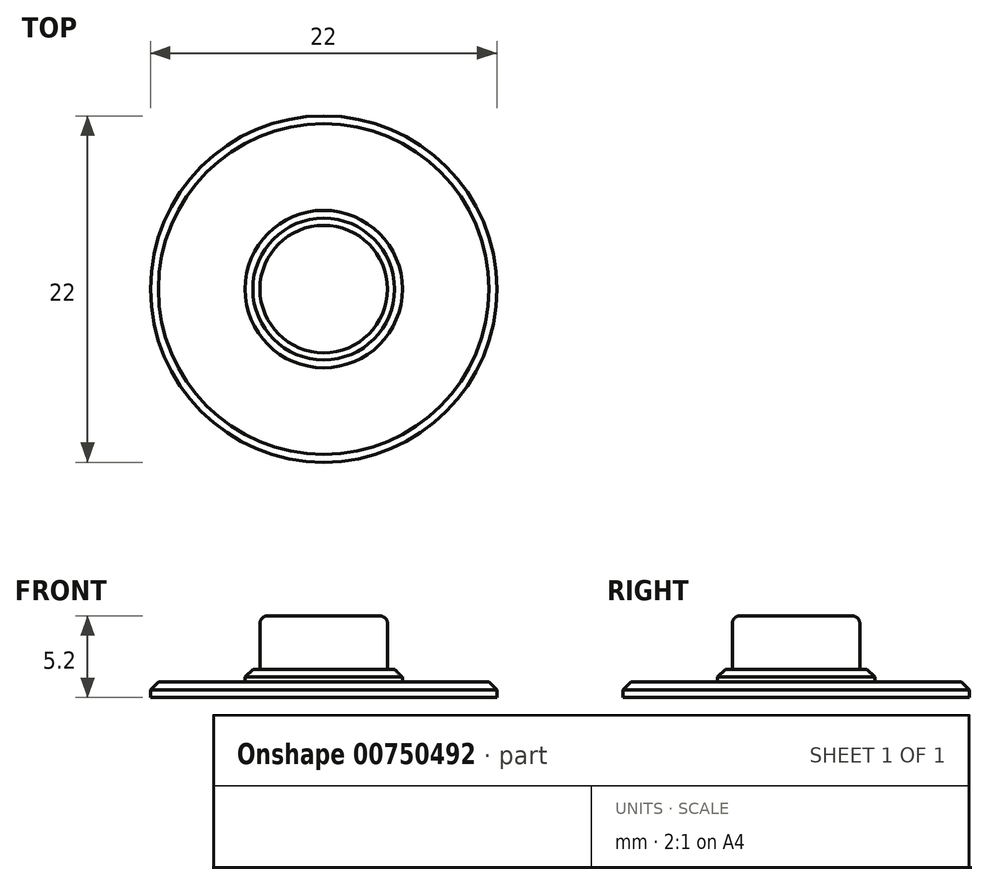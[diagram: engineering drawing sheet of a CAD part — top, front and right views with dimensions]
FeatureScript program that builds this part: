
annotation { "Feature Type Name" : "Feature", "Feature Type Description" : "" }
export const myFeature = defineFeature(function(context is Context, id is Id, definition is map)
    precondition{}
    {
        {
            var Q0;
            Q0=qCreatedBy(makeId("Top.planeOp"),FACE);
            var sketch = newSketch(context, id + "F0", { "sketchPlane" : qUnion([Q0])});
            skCircle(sketch, "E0", {"center": v(0, 0) * mm, "radius": 11 * mm});
            skCircle(sketch, "E1", {"center": v(0, 0) * mm, "radius": 4.05 * mm});
            skCircle(sketch, "E2", {"center": v(0, 0) * mm, "radius": 5 * mm});
            skSolve(sketch);
        }
        {
            var Q0;
            Q0=makeQuery(id+"F0.imprint","IMPRINT",FACE,{"disambiguationData":[TD([[makeQuery(id+"F0.imprint","IMPRINT",EDGE,{"derivedFrom":sQuery(id+"F0.wireOp",EDGE,"E0")}),1.0]])]});
            extrude(context, id + "F1", {"entities" : qUnion([Q0]), "depth" : 1 * mm, "offsetDistance" : 25 * mm});
        }
        {
            var Q0;
            Q0=makeQuery(id+"F1.opExtrude","CAP_EDGE",EDGE,{"disambiguationData":[OSD([sQuery(id+"F0.wireOp",EDGE,"E0")])],"isStart":false});
            chamfer(context, id + "F2", {"entities" : qUnion([Q0]), "width" : 0.5 * mm, "tangentPropagation" : true});
        }
        {
            var Q0;
            Q0=makeQuery(id+"F0.imprint","IMPRINT",FACE,{"disambiguationData":[TD([[makeQuery(id+"F0.imprint","IMPRINT",EDGE,{"derivedFrom":sQuery(id+"F0.wireOp",EDGE,"E1")}),-1.0]])]});
            extrude(context, id + "F3", {"entities" : qUnion([Q0]), "operationType" : NewBodyOperationType.ADD, "depth" : 1.8 * mm, "offsetDistance" : 25 * mm});
        }
        {
            var Q0;
            Q0=makeQuery(id+"F0.imprint","IMPRINT",FACE,{"disambiguationData":[TD([[makeQuery(id+"F0.imprint","IMPRINT",EDGE,{"derivedFrom":sQuery(id+"F0.wireOp",EDGE,"E1")}),1.0]])]});
            extrude(context, id + "F4", {"entities" : qUnion([Q0]), "operationType" : NewBodyOperationType.ADD, "depth" : 5.2 * mm, "offsetDistance" : 25 * mm});
        }
        {
            var Q0;
            Q0=makeQuery(id+"F4.opExtrude","CAP_EDGE",EDGE,{"disambiguationData":[OSD([sQuery(id+"F0.wireOp",EDGE,"E1")])],"isStart":false});
            fillet(context, id + "F5", {"entities" : qUnion([Q0]), "radius" : 0.5 * mm, "tangentPropagation" : true, "allowEdgeOverflow" : false});
        }
        {
            var Q0;
            Q0=makeQuery(id+"F3.opExtrude","CAP_EDGE",EDGE,{"disambiguationData":[OSD([sQuery(id+"F0.wireOp",EDGE,"E2")])],"isStart":false});
            chamfer(context, id + "F6", {"entities" : qUnion([Q0]), "width" : 0.5 * mm, "tangentPropagation" : true});
        }
    });
